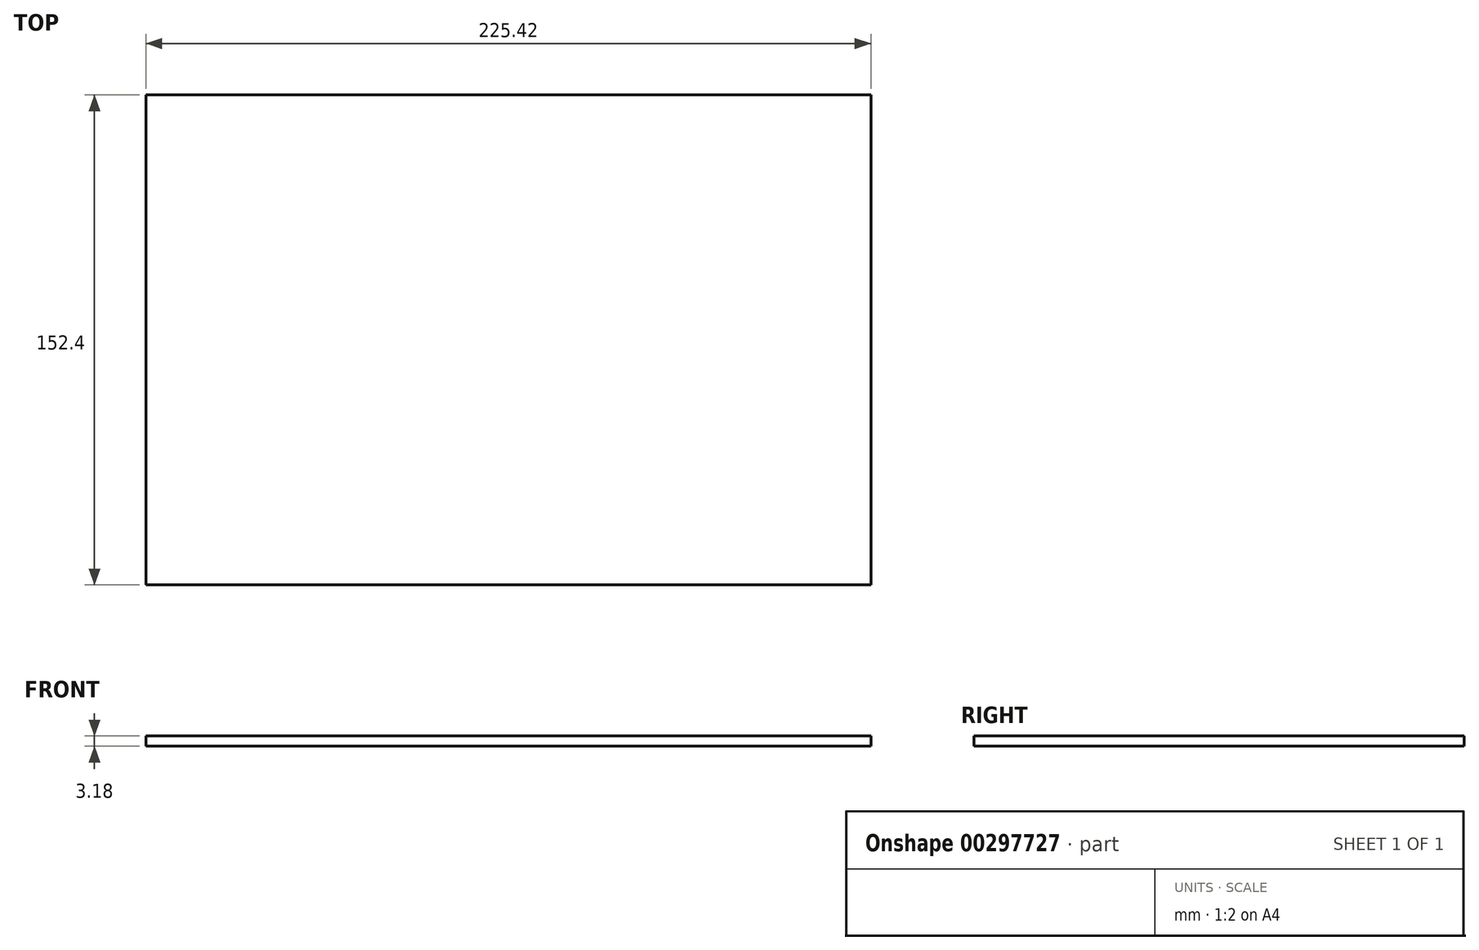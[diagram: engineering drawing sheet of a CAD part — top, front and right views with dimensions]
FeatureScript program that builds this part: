
annotation { "Feature Type Name" : "Feature", "Feature Type Description" : "" }
export const myFeature = defineFeature(function(context is Context, id is Id, definition is map)
    precondition{}
    {
        {
            var Q0;
            Q0=qCreatedBy(makeId("Top.planeOp"),FACE);
            var sketch = newSketch(context, id + "F0", { "sketchPlane" : qUnion([Q0])});
            skLineSegment(sketch, "E0.bottom", {"start": v(112.71, -76.2) * mm, "end": v(-112.71, -76.2) * mm});
            skLineSegment(sketch, "E0.top", {"start": v(112.71, 76.2) * mm, "end": v(-112.71, 76.2) * mm});
            skLineSegment(sketch, "E0.left", {"start": v(112.71, -76.2) * mm, "end": v(112.71, 76.2) * mm});
            skLineSegment(sketch, "E0.right", {"start": v(-112.71, -76.2) * mm, "end": v(-112.71, 76.2) * mm});
            skPoint(sketch, "E0.middle", {"position": v(0, 0) * mm});
            skSolve(sketch);
        }
        {
            var Q0;
            Q0 = qSketchRegion(id + "F0", true);
            extrude(context, id + "F1", {"entities" : qUnion([Q0]), "endBound" : BoundingType.SYMMETRIC, "depth" : 3.17 * mm});
        }
    });
